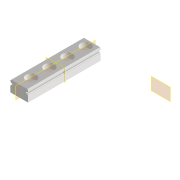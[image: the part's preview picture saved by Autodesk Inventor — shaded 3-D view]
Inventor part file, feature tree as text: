
AUTODESK INVENTOR PART (.ipt)
format: ipt  version: 2022 (Build 260153000, 153)  size: 174,080 bytes
history: native  units: mm
features: plane x3, sketch x2, extrude x1, mirror x1, hole x1, pattern_linear x1, projected_geometry x1
ambient origin geometry x8: Origin, YZ Plane, XZ Plane, XY Plane, X Axis, Y Axis, Z Axis, Center Point
bodies: Solid1 (feature_tree)
feature tree (10):
  plane  "Work Plane1"
  extrude  "Extrusion1"  Depth=0.5mm
  mirror  "Mirror1"
  hole  "Hole1"  [1 undecoded]
  pattern_linear  "Rectangular Pattern1"  Spacing1=6.05mm  [1 undecoded]
  plane  "Work Plane2"
  plane  "Arbeitsebene3"
  sketch  "Sketch1"  dims[d0=0.5mm d1=0.5mm]
  sketch  "Sketch2"  dims[d4=50.0mm d5=0.0mm d6=3.5mm d7=6.0mm d8=7.0mm d9=3.5mm d10=90.0deg d11=8.0mm d12=20.594885mm d13=50.0mm d15=12.5mm d17=6.05mm d18=7.8mm d20=2.67563mm d21=0.5mm d22=1.1mm d23=4.7mm d24=0.227539mm d25=0.228mm d26=0.0mm d27=0.248315mm d28=0.218573mm]
  projected_geometry  "Projected Loop1"
note: 2 required parameter values undecoded (feature->parameter linkage not recoverable at this tier; creation-order binding heuristic only, values carry confidence <= 0.55)
